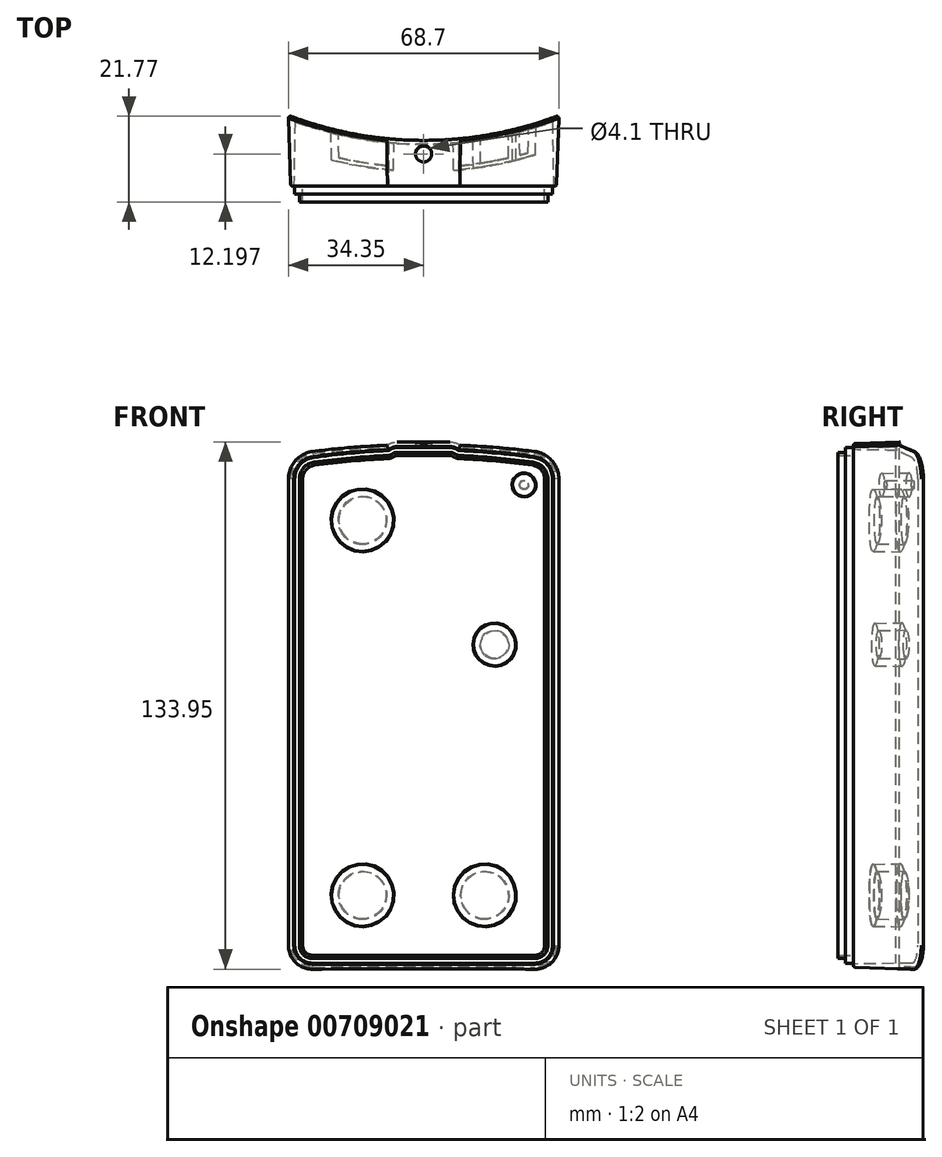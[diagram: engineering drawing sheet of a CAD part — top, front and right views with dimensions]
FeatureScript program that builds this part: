
annotation { "Feature Type Name" : "Feature", "Feature Type Description" : "" }
export const myFeature = defineFeature(function(context is Context, id is Id, definition is map)
    precondition{}
    {
        {
            var Q0;
            Q0=qCreatedBy(makeId("Front.planeOp"),FACE);
            var sketch = newSketch(context, id + "F0", { "sketchPlane" : qUnion([Q0])});
            skLineSegment(sketch, "E0.bottom", {"start": v(4.5, 0) * mm, "end": v(61, 0) * mm});
            skLineSegment(sketch, "E0.left", {"start": v(0, 4.5) * mm, "end": v(0, 123.05) * mm});
            skLineSegment(sketch, "E0.right", {"start": v(65.5, 4.5) * mm, "end": v(65.5, 123.05) * mm});
            skPoint(sketch, "E1.visualSharp", {"position": v(0, 0) * mm});
            skArc(sketch, "E1.filletArc", {"start": v(0, 4.5) * mm, "mid": v(1.32, 1.32) * mm, "end": v(4.5, 0) * mm});
            skPoint(sketch, "E2.visualSharp", {"position": v(65.5, 0) * mm});
            skArc(sketch, "E2.filletArc", {"start": v(61, 0) * mm, "mid": v(64.18, 1.32) * mm, "end": v(65.5, 4.5) * mm});
            skArc(sketch, "E3.filletArc", {"start": v(4.76, 128.5) * mm, "mid": v(1.36, 126.67) * mm, "end": v(0, 123.05) * mm});
            skPoint(sketch, "E4.visualSharp", {"position": v(65.5, 168.18) * mm});
            skArc(sketch, "E4.filletArc", {"start": v(65.5, 123.05) * mm, "mid": v(64.14, 126.67) * mm, "end": v(60.74, 128.5) * mm});
            skArc(sketch, "E5", {"start": v(60.74, 128.5) * mm, "mid": v(51.35, 129.57) * mm, "end": v(41.91, 130.2) * mm});
            skLineSegment(sketch, "E6", {"start": v(26, 131) * mm, "end": v(39.5, 131) * mm});
            skArc(sketch, "E7.trimOffspring", {"start": v(23.59, 130.2) * mm, "mid": v(14.15, 129.57) * mm, "end": v(4.76, 128.5) * mm});
            skLineSegment(sketch, "E8", {"start": v(32.75, 0) * mm, "end": v(32.75, 224.52) * mm, "construction": true});
            skArc(sketch, "E9", {"start": v(26, 131) * mm, "mid": v(25.02, 130.84) * mm, "end": v(24.13, 130.4) * mm});
            skPoint(sketch, "E10.visualSharp", {"position": v(23.91, 130.21) * mm});
            skArc(sketch, "E10.filletArc", {"start": v(23.59, 130.2) * mm, "mid": v(23.87, 130.26) * mm, "end": v(24.13, 130.4) * mm});
            skArc(sketch, "E11.MirrorCS", {"start": v(41.91, 130.2) * mm, "mid": v(41.63, 130.26) * mm, "end": v(41.37, 130.4) * mm});
            skArc(sketch, "E12.MirrorCS", {"start": v(39.5, 131) * mm, "mid": v(40.48, 130.84) * mm, "end": v(41.37, 130.4) * mm});
            skSolve(sketch);
        }
        {
            var Q0;
            Q0=qCreatedBy(makeId("Top.planeOp"),FACE);
            var sketch = newSketch(context, id + "F1", { "sketchPlane" : qUnion([Q0])});
            skArc(sketch, "E13", {"start": v(0, 0) * mm, "mid": v(32.75, -5.75) * mm, "end": v(65.5, 0) * mm});
            skLineSegment(sketch, "E14", {"start": v(0, 0) * mm, "end": v(65.5, 0) * mm});
            skLineSegment(sketch, "E15", {"start": v(0, 0) * mm, "end": v(94.5, 0) * mm, "construction": true});
            skLineSegment(sketch, "E16", {"start": v(94.5, 0) * mm, "end": v(32.75, 0) * mm, "construction": true});
            skLineSegment(sketch, "E17", {"start": v(32.75, 0) * mm, "end": v(32.75, -16.7) * mm, "construction": true});
            skSolve(sketch);
        }
        {
            var Q0;
            Q0=qSketchRegion(id+"F0",true);
            extrude(context, id + "F2", {"entities" : qUnion([Q0]), "depth" : 12.5 * mm, "offsetDistance" : 25 * mm});
        }
        {
            var Q0;
            Q0=qSketchRegion(id+"F1",true);
            extrude(context, id + "F3", {"entities" : qUnion([Q0]), "operationType" : NewBodyOperationType.REMOVE, "endBound" : BoundingType.THROUGH_ALL, "depth" : 25 * mm, "offsetDistance" : 25 * mm});
        }
        {
            var Q0;
            Q0=makeQuery(id+"F2.opExtrude","SWEPT_FACE",FACE,{"disambiguationData":[OSD([sQuery(id+"F0.wireOp",EDGE,"E0.bottom")])]});
            var sketch = newSketch(context, id + "F4", { "sketchPlane" : qUnion([Q0])});
            skLineSegment(sketch, "E18", {"start": v(0, 12.5) * mm, "end": v(0, 10.5) * mm});
            skLineSegment(sketch, "E19", {"start": v(0, 10.5) * mm, "end": v(1.1, 10.5) * mm});
            skLineSegment(sketch, "E20", {"start": v(1.1, 10.5) * mm, "end": v(1.1, 12.5) * mm});
            skLineSegment(sketch, "E21", {"start": v(1.1, 12.5) * mm, "end": v(0, 12.5) * mm});
            skSolve(sketch);
        }
        {
            var Q0;
            Q0=makeQuery(id+"F4.imprint","IMPRINT",FACE,{"disambiguationData":[TD([[makeQuery(id+"F4.imprint","IMPRINT",EDGE,{"derivedFrom":sQuery(id+"F4.wireOp",EDGE,"E18")}),1.0]])]});
            cPlane(context, id + "F5", {"entities" : qUnion([Q0]), "cplaneType" : CPlaneType.OFFSET, "offset" : 50 * mm, "oppositeDirection" : true, "width" : 150 * mm, "height" : 150 * mm});
        }
        {
            var Q0;
            Q0=makeQuery(id+"F2.opExtrude","CAP_FACE",FACE,{"disambiguationData":[OSD([sQuery(id+"F0.wireOp",EDGE,"E0.bottom"),sQuery(id+"F0.wireOp",EDGE,"E0.left"),sQuery(id+"F0.wireOp",EDGE,"E0.right"),sQuery(id+"F0.wireOp",EDGE,"E1.filletArc"),sQuery(id+"F0.wireOp",EDGE,"E2.filletArc"),sQuery(id+"F0.wireOp",EDGE,"E3.filletArc"),sQuery(id+"F0.wireOp",EDGE,"E4.filletArc"),sQuery(id+"F0.wireOp",EDGE,"E5"),sQuery(id+"F0.wireOp",EDGE,"E6"),sQuery(id+"F0.wireOp",EDGE,"4cuLOFSM-Cs9p-uLwk-Nxmp-eiNM5esqOte1"),sQuery(id+"F0.wireOp",EDGE,"qXNs2k06-4niP-ImqC-5Hru-JPzRlnRtqvzY"),sQuery(id+"F0.wireOp",EDGE,"592cab12-c6ad-4f12-8fa5-e9ea6a7a9ab5.filletArc"),sQuery(id+"F0.wireOp",EDGE,"E7.trimOffspring"),sQuery(id+"F0.wireOp",EDGE,"810a662d-7d86-4de4-b075-b749f1e53ed9.filletArc"),sQuery(id+"F0.wireOp",EDGE,"8d541c61-4af1-470d-ac14-312aa46fb37d.filletArc"),sQuery(id+"F0.wireOp",EDGE,"225b199f-dbc8-4900-9de2-33667acb90c7.filletArc")])],"isStart":false});
            shell(context, id + "F6", {"entities" : qUnion([Q0]), "thickness" : 2 * mm});
        }
        {
            var Q0;
            Q0=makeQuery(id+"F2.opExtrude","CAP_FACE",FACE,{"disambiguationData":[OSD([sQuery(id+"F0.wireOp",EDGE,"E0.bottom"),sQuery(id+"F0.wireOp",EDGE,"E0.left"),sQuery(id+"F0.wireOp",EDGE,"E0.right"),sQuery(id+"F0.wireOp",EDGE,"E1.filletArc"),sQuery(id+"F0.wireOp",EDGE,"E2.filletArc"),sQuery(id+"F0.wireOp",EDGE,"E3.filletArc"),sQuery(id+"F0.wireOp",EDGE,"E4.filletArc"),sQuery(id+"F0.wireOp",EDGE,"E5"),sQuery(id+"F0.wireOp",EDGE,"E6"),sQuery(id+"F0.wireOp",EDGE,"E7.trimOffspring"),sQuery(id+"F0.wireOp",EDGE,"E9"),sQuery(id+"F0.wireOp",EDGE,"E10.filletArc"),sQuery(id+"F0.wireOp",EDGE,"E11.MirrorCS"),sQuery(id+"F0.wireOp",EDGE,"E12.MirrorCS")])],"isStart":false});
            var sketch = newSketch(context, id + "F7", { "sketchPlane" : qUnion([Q0])});
            skLineSegment(sketch, "E22.0.0", {"start": v(39.5, 131) * mm, "end": v(26, 131) * mm});
            skArc(sketch, "E22.0.1", {"start": v(26, 131) * mm, "mid": v(25.02, 130.84) * mm, "end": v(24.13, 130.4) * mm});
            skArc(sketch, "E22.0.2", {"start": v(24.13, 130.4) * mm, "mid": v(23.87, 130.26) * mm, "end": v(23.59, 130.2) * mm});
            skArc(sketch, "E22.0.3", {"start": v(23.59, 130.2) * mm, "mid": v(14.15, 129.57) * mm, "end": v(4.76, 128.5) * mm});
            skArc(sketch, "E22.0.4", {"start": v(4.76, 128.5) * mm, "mid": v(1.36, 126.67) * mm, "end": v(0, 123.05) * mm});
            skLineSegment(sketch, "E22.0.5", {"start": v(0, 123.05) * mm, "end": v(0, 4.5) * mm});
            skArc(sketch, "E22.0.6", {"start": v(0, 4.5) * mm, "mid": v(1.32, 1.32) * mm, "end": v(4.5, 0) * mm});
            skLineSegment(sketch, "E22.0.7", {"start": v(4.5, 0) * mm, "end": v(61, 0) * mm});
            skArc(sketch, "E22.0.8", {"start": v(61, 0) * mm, "mid": v(64.18, 1.32) * mm, "end": v(65.5, 4.5) * mm});
            skLineSegment(sketch, "E22.0.9", {"start": v(65.5, 4.5) * mm, "end": v(65.5, 123.05) * mm});
            skArc(sketch, "E22.0.10", {"start": v(65.5, 123.05) * mm, "mid": v(64.14, 126.67) * mm, "end": v(60.74, 128.5) * mm});
            skArc(sketch, "E22.0.11", {"start": v(60.74, 128.5) * mm, "mid": v(51.35, 129.57) * mm, "end": v(41.91, 130.2) * mm});
            skArc(sketch, "E22.0.12", {"start": v(41.91, 130.2) * mm, "mid": v(41.63, 130.26) * mm, "end": v(41.37, 130.4) * mm});
            skArc(sketch, "E22.0.13", {"start": v(41.37, 130.4) * mm, "mid": v(40.48, 130.84) * mm, "end": v(39.5, 131) * mm});
            skArc(sketch, "E23.0", {"start": v(40.66, 129.42) * mm, "mid": v(40.1, 129.7) * mm, "end": v(39.5, 129.8) * mm});
            skArc(sketch, "E23.1", {"start": v(41.86, 129) * mm, "mid": v(41.23, 129.12) * mm, "end": v(40.66, 129.42) * mm});
            skArc(sketch, "E23.2", {"start": v(60.58, 127.31) * mm, "mid": v(51.24, 128.37) * mm, "end": v(41.86, 129) * mm});
            skArc(sketch, "E23.3", {"start": v(4.92, 127.31) * mm, "mid": v(2.26, 125.88) * mm, "end": v(1.2, 123.05) * mm});
            skArc(sketch, "E23.4", {"start": v(23.64, 129) * mm, "mid": v(14.26, 128.37) * mm, "end": v(4.92, 127.31) * mm});
            skArc(sketch, "E23.5", {"start": v(24.84, 129.42) * mm, "mid": v(24.27, 129.12) * mm, "end": v(23.64, 129) * mm});
            skArc(sketch, "E23.6", {"start": v(26, 129.8) * mm, "mid": v(25.4, 129.7) * mm, "end": v(24.84, 129.42) * mm});
            skLineSegment(sketch, "E23.7", {"start": v(1.2, 123.05) * mm, "end": v(1.2, 4.5) * mm});
            skArc(sketch, "E23.8", {"start": v(1.2, 4.5) * mm, "mid": v(2.17, 2.17) * mm, "end": v(4.5, 1.2) * mm});
            skLineSegment(sketch, "E23.9", {"start": v(4.5, 1.2) * mm, "end": v(61, 1.2) * mm});
            skLineSegment(sketch, "E23.10", {"start": v(39.5, 129.8) * mm, "end": v(26, 129.8) * mm});
            skArc(sketch, "E23.11", {"start": v(61, 1.2) * mm, "mid": v(63.33, 2.17) * mm, "end": v(64.3, 4.5) * mm});
            skLineSegment(sketch, "E23.12", {"start": v(64.3, 4.5) * mm, "end": v(64.3, 123.05) * mm});
            skArc(sketch, "E23.13", {"start": v(64.3, 123.05) * mm, "mid": v(63.24, 125.88) * mm, "end": v(60.58, 127.31) * mm});
            skSolve(sketch);
        }
        {
            var Q0;
            Q0=qSketchRegion(id+"F7",true);
            extrude(context, id + "F8", {"entities" : qUnion([Q0]), "operationType" : NewBodyOperationType.REMOVE, "oppositeDirection" : true, "depth" : 2 * mm, "offsetDistance" : 25 * mm});
        }
        {
            var Q0;
            Q0=makeQuery(id+"F6.opShell","OFFSET_EDGE",EDGE,{"disambiguationData":[OSD([sQuery(id+"F0.wireOp",EDGE,"E7.trimOffspring")])]});
            var Q1;
            Q1=makeQuery(id+"F8.boolean.opBoolean","COPY",EDGE,{"derivedFrom":makeQuery(id+"F8.opExtrude","CAP_EDGE",EDGE,{"disambiguationData":[OSD([sQuery(id+"F7.wireOp",EDGE,"E23.4")])],"isStart":true})});
            fillet(context, id + "F9", {"entities" : qUnion([Q0, Q1]), "radius" : .2 * mm, "tangentPropagation" : true, "allowEdgeOverflow" : false});
        }
        {
            var Q0;
            Q0=qCreatedBy(makeId("Front.planeOp"),FACE);
            var sketch = newSketch(context, id + "F10", { "sketchPlane" : qUnion([Q0])});
            skCircle(sketch, "E24", {"center": v(52.88, 68) * mm, "radius": 5.12 * mm});
            skArc(sketch, "E25", {"start": v(16.47, 64.05) * mm, "mid": v(12.44, 73) * mm, "end": v(9.49, 63.64) * mm});
            skArc(sketch, "E26", {"start": v(10.62, 44.32) * mm, "mid": v(14.94, 30.41) * mm, "end": v(17.6, 44.73) * mm});
            skLineSegment(sketch, "E27", {"start": v(12.75, 67.75) * mm, "end": v(14.5, 37.9) * mm, "construction": true});
            skLineSegment(sketch, "E28", {"start": v(16.47, 64.05) * mm, "end": v(17.6, 44.73) * mm});
            skLineSegment(sketch, "E29.MirrorCS", {"start": v(9.49, 63.64) * mm, "end": v(10.62, 44.32) * mm});
            skSolve(sketch);
        }
        {
            var Q0;
            Q0=qSketchRegion(id+"F10",true);
            extrude(context, id + "F11", {"entities" : qUnion([Q0]), "operationType" : NewBodyOperationType.REMOVE, "endBound" : BoundingType.THROUGH_ALL, "depth" : 25 * mm, "offsetDistance" : 25 * mm});
        }
        {
            var Q0;
            Q0=qCreatedBy(makeId("Front.planeOp"),FACE);
            var sketch = newSketch(context, id + "F12", { "sketchPlane" : qUnion([Q0])});
            skLineSegment(sketch, "E30", {"start": v(51.75, 114.46) * mm, "end": v(32.54, 67.75) * mm, "construction": true});
            skArc(sketch, "E31.0.startCap", {"start": v(49.2, 115.5) * mm, "mid": v(52.8, 117) * mm, "end": v(54.3, 113.41) * mm});
            skArc(sketch, "E31.0.endCap", {"start": v(35.09, 66.7) * mm, "mid": v(31.5, 65.2) * mm, "end": v(30, 68.8) * mm});
            skLineSegment(sketch, "E31.0.left", {"start": v(54.3, 113.41) * mm, "end": v(35.09, 66.7) * mm});
            skLineSegment(sketch, "E31.0.right", {"start": v(49.2, 115.5) * mm, "end": v(30, 68.8) * mm});
            skLineSegment(sketch, "E32.0", {"start": v(48.28, 115.89) * mm, "end": v(29.08, 69.18) * mm});
            skArc(sketch, "E32.1", {"start": v(48.28, 115.89) * mm, "mid": v(53.18, 117.93) * mm, "end": v(55.22, 113.03) * mm});
            skLineSegment(sketch, "E32.2", {"start": v(55.22, 113.03) * mm, "end": v(36.01, 66.32) * mm});
            skArc(sketch, "E32.3", {"start": v(36.01, 66.32) * mm, "mid": v(31.12, 64.28) * mm, "end": v(29.08, 69.18) * mm});
            skSolve(sketch);
        }
        {
            var Q0;
            {var subQ0=sQuery(id+"F1.wireOp",EDGE,"E14");var subQ1=sQuery(id+"F1.wireOp",EDGE,"E13");Q0=makeQuery(id+"F3.boolean.opBoolean","MERGE",EDGE,{"derivedFrom":[makeQuery(id+"F2.opExtrude","CAP_EDGE",EDGE,{"disambiguationData":[OSD([sQuery(id+"F0.wireOp",EDGE,"E0.left")])],"isStart":true}),makeQuery(id+"F3.opExtrude","SWEPT_EDGE",EDGE,{"disambiguationData":[OSD([subQ1,subQ0]),TDD([makeQuery(id+"F1.imprint","INTERSECT",VERTEX,{"disambiguationData":[OD(0.0)],"derivedFrom":[subQ1,subQ0]})])]})]});}
            fillet(context, id + "F13", {"entities" : qUnion([Q0]), "radius" : .5 * mm, "tangentPropagation" : true, "allowEdgeOverflow" : false});
        }
        {
            var Q0;
            Q0=qSketchRegion(id+"F12",true);
            var Q1;
            Q1=makeQuery(id+"F3.boolean.opBoolean","COPY",FACE,{"derivedFrom":makeQuery(id+"F3.opExtrude","SWEPT_FACE",FACE,{"disambiguationData":[OSD([sQuery(id+"F1.wireOp",EDGE,"E13")])]})});
            var Q2;
            Q2=makeQuery(id+"F2.opExtrude","SWEPT_BODY",BODY,{"disambiguationData":[OSD([sQuery(id+"F0.wireOp",EDGE,"E0.bottom"),sQuery(id+"F0.wireOp",EDGE,"E0.left"),sQuery(id+"F0.wireOp",EDGE,"E0.right"),sQuery(id+"F0.wireOp",EDGE,"E1.filletArc"),sQuery(id+"F0.wireOp",EDGE,"E2.filletArc"),sQuery(id+"F0.wireOp",EDGE,"E3.filletArc"),sQuery(id+"F0.wireOp",EDGE,"E4.filletArc"),sQuery(id+"F0.wireOp",EDGE,"E5"),sQuery(id+"F0.wireOp",EDGE,"E6"),sQuery(id+"F0.wireOp",EDGE,"E7.trimOffspring"),sQuery(id+"F0.wireOp",EDGE,"E9"),sQuery(id+"F0.wireOp",EDGE,"E10.filletArc"),sQuery(id+"F0.wireOp",EDGE,"E11.MirrorCS"),sQuery(id+"F0.wireOp",EDGE,"E12.MirrorCS")])]});
            var Q3;
            Q3=makeQuery(id+"F3.boolean.opBoolean","COPY",FACE,{"derivedFrom":makeQuery(id+"F3.opExtrude","SWEPT_FACE",FACE,{"disambiguationData":[OSD([sQuery(id+"F1.wireOp",EDGE,"E13")])]})});
            extrude(context, id + "F14", {"entities" : qUnion([Q0]), "operationType" : NewBodyOperationType.ADD, "endBound" : BoundingType.UP_TO_SURFACE, "depth" : 25 * mm, "endBoundEntityFace" : qUnion([Q1]), "endBoundEntityBody" : qUnion([Q2]), "offsetDistance" : 1 * mm, "offsetOppositeDirection" : true, "hasSecondDirection" : true, "secondDirectionBound" : BoundingType.UP_TO_SURFACE, "secondDirectionOppositeDirection" : false, "secondDirectionDepth" : 1 * mm, "secondDirectionBoundEntityFace" : qUnion([Q3]), "hasSecondDirectionOffset" : true, "secondDirectionOffsetDistance" : .5 * mm});
        }
        {
            var Q0;
            Q0=makeQuery(id+"F14.opExtrude","CAP_EDGE",EDGE,{"disambiguationData":[OSD([sQuery(id+"F12.wireOp",EDGE,"E31.0.left")])],"isStart":true});
            var Q1;
            Q1=makeQuery(id+"F14.opExtrude","CAP_EDGE",EDGE,{"disambiguationData":[OSD([sQuery(id+"F12.wireOp",EDGE,"E32.2")])],"isStart":true});
            fillet(context, id + "F15", {"entities" : qUnion([Q0, Q1]), "radius" : .5 * mm, "tangentPropagation" : true, "allowEdgeOverflow" : false});
        }
        {
            var Q0;
            Q0=qCreatedBy(makeId("Front.planeOp"),FACE);
            var sketch = newSketch(context, id + "F16", { "sketchPlane" : qUnion([Q0])});
            skCircle(sketch, "E33", {"center": v(51.75, 114.46) * mm, "radius": 0.75 * mm});
            skLineSegment(sketch, "E34.0", {"start": v(51.75, 114.46) * mm, "end": v(32.54, 67.75) * mm, "construction": true});
            skSolve(sketch);
        }
        {
            var Q0;
            Q0=makeQuery(id+"F16.imprint","IMPRINT",FACE,{"disambiguationData":[TD([[makeQuery(id+"F16.imprint","IMPRINT",EDGE,{"derivedFrom":sQuery(id+"F16.wireOp",EDGE,"E33")}),1.0]])]});
            var Q1;
            Q1=qConstructionFilter(qBodyType(qCreatedBy(id+"F16",EDGE),BodyType.WIRE),ConstructionObject.NO);
            extrude(context, id + "F17", {"entities" : qUnion([Q0]), "operationType" : NewBodyOperationType.REMOVE, "surfaceEntities" : qUnion([Q1]), "endBound" : BoundingType.THROUGH_ALL, "depth" : 25 * mm, "offsetDistance" : 25 * mm});
        }
        {
            var Q0;
            Q0=qCreatedBy(makeId("Top.planeOp"),FACE);
            var sketch = newSketch(context, id + "F18", { "sketchPlane" : qUnion([Q0])});
            skLineSegment(sketch, "E35.0", {"start": v(-0.5, -7.5) * mm, "end": v(-0.5, 1.21) * mm});
            skLineSegment(sketch, "E35.1", {"start": v(66, -7.57) * mm, "end": v(66, 1.14) * mm});
            skLineSegment(sketch, "E36", {"start": v(32.75, -4) * mm, "end": v(32.75, 0.99) * mm, "construction": true});
            skPoint(sketch, "E36.startSnap0", {"position": v(32.75, -4) * mm});
            skArc(sketch, "E37.0", {"start": v(66, 1.14) * mm, "mid": v(32.75, -4.75) * mm, "end": v(-0.5, 1.21) * mm});
            skSolve(sketch);
        }
        {
            var Q0;
            Q0=makeQuery(id+"F8.boolean.opBoolean","COPY",FACE,{"derivedFrom":makeQuery(id+"F8.opExtrude","CAP_FACE",FACE,{"disambiguationData":[OSD([sQuery(id+"F7.wireOp",EDGE,"E22.0.0"),sQuery(id+"F7.wireOp",EDGE,"E22.0.1"),sQuery(id+"F7.wireOp",EDGE,"E22.0.2"),sQuery(id+"F7.wireOp",EDGE,"E22.0.3"),sQuery(id+"F7.wireOp",EDGE,"E22.0.4"),sQuery(id+"F7.wireOp",EDGE,"E22.0.5"),sQuery(id+"F7.wireOp",EDGE,"E22.0.6"),sQuery(id+"F7.wireOp",EDGE,"E22.0.7"),sQuery(id+"F7.wireOp",EDGE,"E22.0.8"),sQuery(id+"F7.wireOp",EDGE,"E22.0.9"),sQuery(id+"F7.wireOp",EDGE,"E22.0.10"),sQuery(id+"F7.wireOp",EDGE,"E22.0.11"),sQuery(id+"F7.wireOp",EDGE,"E22.0.12"),sQuery(id+"F7.wireOp",EDGE,"E22.0.13"),sQuery(id+"F7.wireOp",EDGE,"E23.0"),sQuery(id+"F7.wireOp",EDGE,"E23.1"),sQuery(id+"F7.wireOp",EDGE,"E23.2"),sQuery(id+"F7.wireOp",EDGE,"E23.3"),sQuery(id+"F7.wireOp",EDGE,"E23.4"),sQuery(id+"F7.wireOp",EDGE,"E23.5"),sQuery(id+"F7.wireOp",EDGE,"E23.6"),sQuery(id+"F7.wireOp",EDGE,"E23.7"),sQuery(id+"F7.wireOp",EDGE,"E23.8"),sQuery(id+"F7.wireOp",EDGE,"E23.9"),sQuery(id+"F7.wireOp",EDGE,"E23.10"),sQuery(id+"F7.wireOp",EDGE,"E23.11"),sQuery(id+"F7.wireOp",EDGE,"E23.12"),sQuery(id+"F7.wireOp",EDGE,"E23.13")])],"isStart":false})});
            cPlane(context, id + "F19", {"entities" : qUnion([Q0]), "cplaneType" : CPlaneType.OFFSET, "offset" : 2 * mm, "oppositeDirection" : true, "width" : 150 * mm, "height" : 150 * mm});
        }
        {
            var Q0;
            Q0=qCreatedBy(id+"F19.planeOp",FACE);
            var sketch = newSketch(context, id + "F20", { "sketchPlane" : qUnion([Q0])});
            skLineSegment(sketch, "E38.0.0", {"start": v(39.5, 131) * mm, "end": v(26, 131) * mm});
            skArc(sketch, "E38.0.1", {"start": v(26, 131) * mm, "mid": v(25.02, 130.84) * mm, "end": v(24.13, 130.4) * mm});
            skArc(sketch, "E38.0.2", {"start": v(24.13, 130.4) * mm, "mid": v(23.87, 130.26) * mm, "end": v(23.59, 130.2) * mm});
            skArc(sketch, "E38.0.3", {"start": v(23.59, 130.2) * mm, "mid": v(14.15, 129.57) * mm, "end": v(4.76, 128.5) * mm});
            skArc(sketch, "E38.0.4", {"start": v(4.76, 128.5) * mm, "mid": v(1.36, 126.67) * mm, "end": v(0, 123.05) * mm});
            skLineSegment(sketch, "E38.0.5", {"start": v(0, 123.05) * mm, "end": v(0, 4.5) * mm});
            skArc(sketch, "E38.0.6", {"start": v(0, 4.5) * mm, "mid": v(1.32, 1.32) * mm, "end": v(4.5, 0) * mm});
            skLineSegment(sketch, "E38.0.7", {"start": v(4.5, 0) * mm, "end": v(61, 0) * mm});
            skArc(sketch, "E38.0.8", {"start": v(61, 0) * mm, "mid": v(64.18, 1.32) * mm, "end": v(65.5, 4.5) * mm});
            skLineSegment(sketch, "E38.0.9", {"start": v(65.5, 4.5) * mm, "end": v(65.5, 123.05) * mm});
            skArc(sketch, "E38.0.10", {"start": v(65.5, 123.05) * mm, "mid": v(64.14, 126.67) * mm, "end": v(60.74, 128.5) * mm});
            skArc(sketch, "E38.0.11", {"start": v(60.74, 128.5) * mm, "mid": v(51.35, 129.57) * mm, "end": v(41.91, 130.2) * mm});
            skArc(sketch, "E38.0.12", {"start": v(41.91, 130.2) * mm, "mid": v(41.63, 130.26) * mm, "end": v(41.37, 130.4) * mm});
            skArc(sketch, "E38.0.13", {"start": v(41.37, 130.4) * mm, "mid": v(40.48, 130.84) * mm, "end": v(39.5, 131) * mm});
            skLineSegment(sketch, "E39.0", {"start": v(4.5, -1) * mm, "end": v(61, -1) * mm});
            skArc(sketch, "E39.1", {"start": v(41.96, 131.2) * mm, "mid": v(40.8, 131.8) * mm, "end": v(39.5, 132) * mm});
            skArc(sketch, "E39.2", {"start": v(60.88, 129.5) * mm, "mid": v(51.44, 130.56) * mm, "end": v(41.96, 131.2) * mm});
            skArc(sketch, "E39.3", {"start": v(66.5, 123.05) * mm, "mid": v(64.9, 127.32) * mm, "end": v(60.88, 129.5) * mm});
            skLineSegment(sketch, "E39.4", {"start": v(66.5, 4.5) * mm, "end": v(66.5, 123.05) * mm});
            skLineSegment(sketch, "E39.5", {"start": v(39.5, 132) * mm, "end": v(26, 132) * mm});
            skArc(sketch, "E39.6", {"start": v(61, -1) * mm, "mid": v(64.89, 0.61) * mm, "end": v(66.5, 4.5) * mm});
            skArc(sketch, "E39.7", {"start": v(26, 132) * mm, "mid": v(24.7, 131.8) * mm, "end": v(23.54, 131.2) * mm});
            skArc(sketch, "E39.8", {"start": v(23.54, 131.2) * mm, "mid": v(14.06, 130.56) * mm, "end": v(4.62, 129.5) * mm});
            skArc(sketch, "E39.9", {"start": v(4.62, 129.5) * mm, "mid": v(0.6, 127.32) * mm, "end": v(-1, 123.05) * mm});
            skLineSegment(sketch, "E39.10", {"start": v(-1, 123.05) * mm, "end": v(-1, 4.5) * mm});
            skArc(sketch, "E39.11", {"start": v(-1, 4.5) * mm, "mid": v(0.61, 0.61) * mm, "end": v(4.5, -1) * mm});
            skArc(sketch, "E40.0", {"start": v(4.72, 128.75) * mm, "mid": v(1.17, 126.83) * mm, "end": v(-0.25, 123.05) * mm});
            skLineSegment(sketch, "E40.1", {"start": v(65.75, 4.5) * mm, "end": v(65.75, 123.05) * mm});
            skArc(sketch, "E40.2", {"start": v(61, -0.25) * mm, "mid": v(64.36, 1.14) * mm, "end": v(65.75, 4.5) * mm});
            skLineSegment(sketch, "E40.3", {"start": v(4.5, -0.25) * mm, "end": v(61, -0.25) * mm});
            skArc(sketch, "E40.4", {"start": v(-0.25, 4.5) * mm, "mid": v(1.14, 1.14) * mm, "end": v(4.5, -0.25) * mm});
            skArc(sketch, "E40.5", {"start": v(65.75, 123.05) * mm, "mid": v(64.33, 126.83) * mm, "end": v(60.78, 128.75) * mm});
            skLineSegment(sketch, "E40.6", {"start": v(-0.25, 123.05) * mm, "end": v(-0.25, 4.5) * mm});
            skArc(sketch, "E40.7", {"start": v(60.78, 128.75) * mm, "mid": v(51.25, 129.82) * mm, "end": v(41.68, 130.46) * mm});
            skArc(sketch, "E40.8", {"start": v(41.68, 130.46) * mm, "mid": v(40.66, 131.05) * mm, "end": v(39.5, 131.25) * mm});
            skLineSegment(sketch, "E40.9", {"start": v(39.5, 131.25) * mm, "end": v(26, 131.25) * mm});
            skArc(sketch, "E40.10", {"start": v(26, 131.25) * mm, "mid": v(24.84, 131.05) * mm, "end": v(23.82, 130.46) * mm});
            skArc(sketch, "E40.11", {"start": v(23.82, 130.46) * mm, "mid": v(14.25, 129.82) * mm, "end": v(4.72, 128.75) * mm});
            skSolve(sketch);
        }
        {
            var Q0;
            Q0=makeQuery(id+"F20.imprint","IMPRINT",FACE,{"disambiguationData":[TD([[makeQuery(id+"F20.imprint","IMPRINT",EDGE,{"derivedFrom":sQuery(id+"F20.wireOp",EDGE,"E38.0.0")}),-1.0]])]});
            var Q1;
            Q1=makeQuery(id+"F20.imprint","IMPRINT",FACE,{"disambiguationData":[TD([[makeQuery(id+"F20.imprint","IMPRINT",EDGE,{"derivedFrom":sQuery(id+"F20.wireOp",EDGE,"E38.0.0")}),1.0]])]});
            var Q2;
            Q2=makeQuery(id+"F20.imprint","IMPRINT",FACE,{"disambiguationData":[TD([[makeQuery(id+"F20.imprint","IMPRINT",EDGE,{"derivedFrom":sQuery(id+"F20.wireOp",EDGE,"E39.0")}),1.0]])]});
            extrude(context, id + "F21", {"entities" : qUnion([Q0, Q1, Q2]), "oppositeDirection" : true, "depth" : 18 * mm, "offsetDistance" : 25 * mm, "hasDraft" : true, "draftAngle" : 2 * degree});
        }
        {
            var Q0;
            Q0=qCreatedBy(makeId("Top.planeOp"),FACE);
            var sketch = newSketch(context, id + "F22", { "sketchPlane" : qUnion([Q0])});
            skLineSegment(sketch, "E41.0.0", {"start": v(61, -8.5) * mm, "end": v(4.5, -8.5) * mm, "construction": true});
            skLineSegment(sketch, "E41.0.1", {"start": v(4.5, 9.5) * mm, "end": v(4.5, -8.5) * mm, "construction": true});
            skLineSegment(sketch, "E41.0.2", {"start": v(4.5, 9.5) * mm, "end": v(61, 9.5) * mm, "construction": true});
            skLineSegment(sketch, "E41.0.3", {"start": v(61, 9.5) * mm, "end": v(61, -8.5) * mm, "construction": true});
            skLineSegment(sketch, "E41.1.0", {"start": v(66.5, -8.5) * mm, "end": v(61, -8.5) * mm, "construction": true});
            skLineSegment(sketch, "E41.1.1", {"start": v(61, 9.5) * mm, "end": v(61, -8.5) * mm, "construction": true});
            skLineSegment(sketch, "E41.1.2", {"start": v(61, 9.5) * mm, "end": v(67.13, 9.5) * mm, "construction": true});
            skLineSegment(sketch, "E41.1.3", {"start": v(67.13, 9.5) * mm, "end": v(66.5, -8.5) * mm, "construction": true});
            skLineSegment(sketch, "E41.2.0", {"start": v(4.5, -8.5) * mm, "end": v(-1, -8.5) * mm, "construction": true});
            skLineSegment(sketch, "E41.2.1", {"start": v(-1.63, 9.5) * mm, "end": v(-1, -8.5) * mm, "construction": true});
            skLineSegment(sketch, "E41.2.2", {"start": v(-1.63, 9.5) * mm, "end": v(4.5, 9.5) * mm, "construction": true});
            skLineSegment(sketch, "E41.2.3", {"start": v(4.5, 9.5) * mm, "end": v(4.5, -8.5) * mm, "construction": true});
            skArc(sketch, "E42", {"start": v(-1.63, 9.5) * mm, "mid": v(32.75, 3.14) * mm, "end": v(67.13, 9.5) * mm});
            skLineSegment(sketch, "E43", {"start": v(-1.63, 9.5) * mm, "end": v(67.13, 9.5) * mm});
            skSolve(sketch);
        }
        {
            var Q0;
            Q0=makeQuery(id+"F22.imprint","IMPRINT",FACE,{"disambiguationData":[TD([[makeQuery(id+"F22.imprint","IMPRINT",EDGE,{"derivedFrom":sQuery(id+"F22.wireOp",EDGE,"E42")}),1.0]])]});
            extrude(context, id + "F23", {"entities" : qUnion([Q0]), "operationType" : NewBodyOperationType.REMOVE, "endBound" : BoundingType.THROUGH_ALL, "oppositeDirection" : true, "depth" : 25 * mm, "offsetDistance" : 25 * mm, "hasSecondDirection" : true, "secondDirectionBound" : BoundingType.THROUGH_ALL, "secondDirectionOppositeDirection" : false, "secondDirectionDepth" : 25 * mm});
        }
        {
            var Q0;
            Q0=qCreatedBy(makeId("Top.planeOp"),FACE);
            cPlane(context, id + "F24", {"entities" : qUnion([Q0]), "cplaneType" : CPlaneType.OFFSET, "offset" : 6.5 * mm, "oppositeDirection" : true, "width" : 150 * mm, "height" : 150 * mm});
        }
        {
            var Q0;
            Q0=sQuery(id+"F18.wireOp",EDGE,"E37.0");
            extrude(context, id + "F25", {"bodyType" : ToolBodyType.SURFACE, "surfaceEntities" : qUnion([Q0]), "oppositeDirection" : true, "depth" : 5 * mm, "offsetDistance" : 25 * mm, "hasSecondDirection" : true, "secondDirectionOppositeDirection" : false, "secondDirectionDepth" : 150 * mm});
        }
        {
            var Q0;
            Q0=qCreatedBy(id+"F24.planeOp",FACE);
            var sketch = newSketch(context, id + "F26", { "sketchPlane" : qUnion([Q0])});
            skArc(sketch, "E44.0", {"start": v(-0.75, 1.9) * mm, "mid": v(32.75, -4.13) * mm, "end": v(66.25, 1.9) * mm});
            skLineSegment(sketch, "E45.0.0", {"start": v(39.5, -10.5) * mm, "end": v(39.5, -6.01) * mm, "construction": true});
            skArc(sketch, "E45.0.1", {"start": v(39.5, -6.01) * mm, "mid": v(32.75, -6.25) * mm, "end": v(26, -6.01) * mm, "construction": true});
            skLineSegment(sketch, "E45.0.2", {"start": v(26, -6.01) * mm, "end": v(26, -10.5) * mm, "construction": true});
            skLineSegment(sketch, "E45.0.3", {"start": v(26, -10.5) * mm, "end": v(39.5, -10.5) * mm, "construction": true});
            skLineSegment(sketch, "E46", {"start": v(32.75, -10.5) * mm, "end": v(32.75, 21.11) * mm, "construction": true});
            skPoint(sketch, "E46.endSnap0", {"position": v(32.75, -6.25) * mm});
            skSolve(sketch);
        }
        {
            var Q0;
            Q0=sQuery(id+"F26.wireOp",EDGE,"E44.0");
            extrude(context, id + "F27", {"bodyType" : ToolBodyType.SURFACE, "surfaceEntities" : qUnion([Q0]), "depth" : 147.2 * mm, "offsetDistance" : 25 * mm});
        }
        {
            var Q0;
            Q0=qCreatedBy(makeId("Front.planeOp"),FACE);
            cPlane(context, id + "F28", {"entities" : qUnion([Q0]), "cplaneType" : CPlaneType.OFFSET, "offset" : 10 * mm, "oppositeDirection" : true, "width" : 150 * mm, "height" : 150 * mm});
        }
        {
            var Q0;
            Q0=sQuery(id+"F22.wireOp",EDGE,"E42");
            extrude(context, id + "F29", {"bodyType" : ToolBodyType.SURFACE, "surfaceEntities" : qUnion([Q0]), "oppositeDirection" : true, "depth" : 10 * mm, "offsetDistance" : 25 * mm, "hasSecondDirection" : true, "secondDirectionOppositeDirection" : false, "secondDirectionDepth" : 141.6 * mm});
        }
        {
            var Q0;
            Q0=makeQuery(id+"F29.opExtrude","SWEPT_BODY",BODY,{"disambiguationData":[OSD([sQuery(id+"F22.wireOp",EDGE,"E42")])]});
            transform(context, id + "F30", {"entities" : qUnion([Q0]), "transformType" : TransformType.TRANSLATION_3D, "dx" : 0 * mm, "dy" : -1 * mm, "dz" : 0 * mm, "makeCopy" : false});
        }
        {
            var Q0;
            Q0=qCreatedBy(makeId("Top.planeOp"),FACE);
            cPlane(context, id + "F31", {"entities" : qUnion([Q0]), "cplaneType" : CPlaneType.OFFSET, "offset" : 140.2 * mm, "width" : 150 * mm, "height" : 150 * mm});
        }
        {
            var Q0;
            Q0=qCreatedBy(id+"F31.planeOp",FACE);
            var sketch = newSketch(context, id + "F32", { "sketchPlane" : qUnion([Q0])});
            skLineSegment(sketch, "E47.0.0", {"start": v(26, 3.38) * mm, "end": v(26, -6.5) * mm, "construction": true});
            skLineSegment(sketch, "E47.0.1", {"start": v(26, -6.5) * mm, "end": v(39.5, -6.5) * mm, "construction": true});
            skLineSegment(sketch, "E47.0.2", {"start": v(39.5, 3.38) * mm, "end": v(39.5, -6.5) * mm, "construction": true});
            skArc(sketch, "E47.0.3", {"start": v(36, 3.2) * mm, "mid": v(32.75, 3.14) * mm, "end": v(29.5, 3.2) * mm});
            skLineSegment(sketch, "E48", {"start": v(32.75, -6.5) * mm, "end": v(32.75, 3.14) * mm, "construction": true});
            skLineSegment(sketch, "E49", {"start": v(29.5, 3.2) * mm, "end": v(29.5, -0.1) * mm});
            skLineSegment(sketch, "E50.MirrorCS", {"start": v(36, 3.2) * mm, "end": v(36, -0.1) * mm});
            skArc(sketch, "E51", {"start": v(29.5, -0.1) * mm, "mid": v(32.75, -3.36) * mm, "end": v(36, -0.1) * mm});
            skSolve(sketch);
        }
        {
            var Q0;
            Q0=makeQuery(id+"F21.opExtrude","CAP_EDGE",EDGE,{"disambiguationData":[OSD([sQuery(id+"F20.wireOp",EDGE,"E39.2")])],"isStart":true});
            var Q1;
            Q1=makeQuery(id+"F21.opExtrude","CAP_EDGE",EDGE,{"disambiguationData":[OSD([sQuery(id+"F20.wireOp",EDGE,"E39.1")])],"isStart":true});
            fillet(context, id + "F33", {"entities" : qUnion([Q0, Q1]), "radius" : .5 * mm, "tangentPropagation" : true, "allowEdgeOverflow" : false});
        }
        {
            var Q0;
            Q0=qCreatedBy(makeId("Front.planeOp"),FACE);
            var sketch = newSketch(context, id + "F34", { "sketchPlane" : qUnion([Q0])});
            skArc(sketch, "E52.0", {"start": v(36, 115.24) * mm, "mid": v(32.75, 115.26) * mm, "end": v(29.5, 115.24) * mm});
            skArc(sketch, "E53", {"start": v(29.5, 115.24) * mm, "mid": v(32.75, 112.01) * mm, "end": v(36, 115.24) * mm});
            skSolve(sketch);
        }
        {
            var Q0;
            Q0=makeQuery(id+"F20.imprint","IMPRINT",FACE,{"disambiguationData":[TD([[makeQuery(id+"F20.imprint","IMPRINT",EDGE,{"derivedFrom":sQuery(id+"F20.wireOp",EDGE,"E38.0.0")}),-1.0]])]});
            var Q1;
            Q1=makeQuery(id+"F20.imprint","IMPRINT",FACE,{"disambiguationData":[TD([[makeQuery(id+"F20.imprint","IMPRINT",EDGE,{"derivedFrom":sQuery(id+"F20.wireOp",EDGE,"E38.0.0")}),1.0]])]});
            var Q2;
            Q2=makeQuery(id+"F29.opExtrude","SWEPT_FACE",FACE,{"disambiguationData":[OSD([sQuery(id+"F22.wireOp",EDGE,"E42")])]});
            extrude(context, id + "F35", {"entities" : qUnion([Q0, Q1]), "operationType" : NewBodyOperationType.REMOVE, "endBound" : BoundingType.UP_TO_SURFACE, "oppositeDirection" : true, "depth" : 25 * mm, "endBoundEntityFace" : qUnion([Q2]), "offsetDistance" : 25 * mm, "hasDraft" : true, "draftAngle" : 1 * degree, "draftPullDirection" : true});
        }
        {
            var Q0;
            Q0=qCreatedBy(makeId("Front.planeOp"),FACE);
            cPlane(context, id + "F36", {"entities" : qUnion([Q0]), "cplaneType" : CPlaneType.OFFSET, "offset" : 25 * mm, "width" : 150 * mm, "height" : 150 * mm});
        }
        {
            var Q0;
            Q0=qCreatedBy(id+"F36.planeOp",FACE);
            var sketch = newSketch(context, id + "F37", { "sketchPlane" : qUnion([Q0])});
            skCircle(sketch, "E54", {"center": v(48.25, 17.25) * mm, "radius": 7.5 * mm});
            skLineSegment(sketch, "E55.0", {"start": v(4.5, -0.52) * mm, "end": v(61, -0.52) * mm, "construction": true});
            skLineSegment(sketch, "E56", {"start": v(32.75, -0.52) * mm, "end": v(32.75, 50.45) * mm, "construction": true});
            skCircle(sketch, "E57.MirrorC", {"center": v(17.25, 17.25) * mm, "radius": 7.5 * mm});
            skCircle(sketch, "E58.MirrorC", {"center": v(17.25, 112.52) * mm, "radius": 7.5 * mm});
            skCircle(sketch, "E59", {"center": v(50.75, 80.95) * mm, "radius": 5 * mm});
            skCircle(sketch, "E60", {"center": v(58.25, 121.52) * mm, "radius": 2.5 * mm});
            skSolve(sketch);
        }
        {
            var Q0;
            Q0=qSketchRegion(id+"F37",true);
            var Q1;
            Q1=makeQuery(id+"F21.opExtrude","SWEPT_BODY",BODY,{"disambiguationData":[OSD([sQuery(id+"F20.wireOp",EDGE,"E39.0"),sQuery(id+"F20.wireOp",EDGE,"E39.1"),sQuery(id+"F20.wireOp",EDGE,"E39.2"),sQuery(id+"F20.wireOp",EDGE,"E39.3"),sQuery(id+"F20.wireOp",EDGE,"E39.4"),sQuery(id+"F20.wireOp",EDGE,"E39.5"),sQuery(id+"F20.wireOp",EDGE,"E39.6"),sQuery(id+"F20.wireOp",EDGE,"E39.7"),sQuery(id+"F20.wireOp",EDGE,"E39.8"),sQuery(id+"F20.wireOp",EDGE,"E39.9"),sQuery(id+"F20.wireOp",EDGE,"E39.10"),sQuery(id+"F20.wireOp",EDGE,"E39.11")])]});
            var Q2;
            Q2=makeQuery(id+"F25.opExtrude","SWEPT_FACE",FACE,{"disambiguationData":[OSD([sQuery(id+"F18.wireOp",EDGE,"E37.0")])]});
            extrude(context, id + "F38", {"entities" : qUnion([Q0]), "operationType" : NewBodyOperationType.ADD, "endBound" : BoundingType.UP_TO_BODY, "oppositeDirection" : true, "depth" : 25 * mm, "endBoundEntityBody" : qUnion([Q1]), "offsetDistance" : 25 * mm, "hasDraft" : true, "draftAngle" : 1 * degree, "hasSecondDirection" : true, "secondDirectionBound" : BoundingType.UP_TO_SURFACE, "secondDirectionOppositeDirection" : true, "secondDirectionDepth" : 25 * mm, "secondDirectionBoundEntityFace" : qUnion([Q2])});
        }
        {
            var Q0;
            Q0=qCreatedBy(makeId("Front.planeOp"),FACE);
            cPlane(context, id + "F39", {"entities" : qUnion([Q0]), "cplaneType" : CPlaneType.OFFSET, "offset" : 25 * mm, "oppositeDirection" : true, "width" : 150 * mm, "height" : 150 * mm});
        }
        {
            var Q0;
            Q0=qCreatedBy(id+"F39.planeOp",FACE);
            var sketch = newSketch(context, id + "F40", { "sketchPlane" : qUnion([Q0])});
            skCircle(sketch, "E61.0", {"center": v(17.25, 112.52) * mm, "radius": 6.5 * mm});
            skCircle(sketch, "E61.1", {"center": v(58.25, 121.52) * mm, "radius": 1.5 * mm});
            skCircle(sketch, "E61.2", {"center": v(50.75, 80.95) * mm, "radius": 4 * mm});
            skCircle(sketch, "E61.3", {"center": v(48.25, 17.25) * mm, "radius": 6.5 * mm});
            skLineSegment(sketch, "E61.4", {"start": v(32.75, -0.52) * mm, "end": v(32.75, 50.45) * mm, "construction": true});
            skCircle(sketch, "E61.5", {"center": v(17.25, 17.25) * mm, "radius": 6.5 * mm});
            skLineSegment(sketch, "E61.6", {"start": v(4.5, -0.52) * mm, "end": v(61, -0.52) * mm, "construction": true});
            skSolve(sketch);
        }
        {
            var Q0;
            Q0=qSketchRegion(id+"F40",true);
            var Q1;
            Q1=makeQuery(id+"F38.opExtrude","CAP_FACE",FACE,{"disambiguationData":[OSD([sQuery(id+"F37.wireOp",EDGE,"E58.MirrorC")]),topologyDisambiguationEdgeConnected([makeQuery(id+"F25.opExtrude","SWEPT_FACE",FACE,{"disambiguationData":[OSD([sQuery(id+"F18.wireOp",EDGE,"E37.0")])]})])],"isStart":false});
            extrude(context, id + "F41", {"entities" : qUnion([Q0]), "operationType" : NewBodyOperationType.REMOVE, "endBound" : BoundingType.UP_TO_SURFACE, "depth" : 25 * mm, "endBoundEntityFace" : qUnion([Q1]), "hasOffset" : true, "offsetDistance" : 1 * mm, "hasDraft" : true, "draftAngle" : 1 * degree, "draftPullDirection" : true});
        }
        {
            var Q0;
            Q0=makeQuery(id+"F23.boolean.opBoolean","INTERSECT",EDGE,{"derivedFrom":[makeQuery(id+"F21.opExtrude","SWEPT_FACE",FACE,{"disambiguationData":[OSD([sQuery(id+"F20.wireOp",EDGE,"E39.0")])]}),makeQuery(id+"F23.opExtrude","SWEPT_FACE",FACE,{"disambiguationData":[OSD([sQuery(id+"F22.wireOp",EDGE,"E42")])]})]});
            fillet(context, id + "F42", {"entities" : qUnion([Q0]), "radius" : .5 * mm, "tangentPropagation" : true, "allowEdgeOverflow" : false});
        }
        {
            var Q0;
            Q0=makeQuery(id+"F35.boolean.opBoolean","COPY",FACE,{"derivedFrom":makeQuery(id+"F35.opExtrude","SWEPT_FACE",FACE,{"disambiguationData":[OSD([sQuery(id+"F20.wireOp",EDGE,"E40.9")])]})});
            var sketch = newSketch(context, id + "F43", { "sketchPlane" : qUnion([Q0])});
            skCircle(sketch, "E62", {"center": v(32.75, 2.6) * mm, "radius": 2.45 * mm, "construction": true});
            skEllipticalArc(sketch, "E63.0", {"construction": true});
            skLineSegment(sketch, "E64", {"start": v(32.75, 0.15) * mm, "end": v(32.75, 13.43) * mm, "construction": true});
            skCircle(sketch, "E65", {"center": v(32.75, 2.6) * mm, "radius": 2.05 * mm});
            const initialGuessF43  = {"E63.0": [0.03275, -0.09596723813539623, 0, -1, 0.09611463872501952, 0.0961, 3.0712954359205873, 3.211889871258989]};
            skSetInitialGuess(sketch, initialGuessF43);
            skSolve(sketch);
        }
        {
            var Q0;
            Q0 = qSketchRegion(id + "F43", true);
            extrude(context, id + "F44", {"entities" : qUnion([Q0]), "operationType" : NewBodyOperationType.REMOVE, "oppositeDirection" : true, "depth" : 25 * mm, "offsetDistance" : 25 * mm, "hasSecondDirection" : true, "secondDirectionOppositeDirection" : false, "secondDirectionDepth" : 25 * mm});
        }
        {
            var Q0;
            Q0=makeQuery(id+"F21.opExtrude","CAP_FACE",FACE,{"disambiguationData":[OSD([sQuery(id+"F20.wireOp",EDGE,"E39.0"),sQuery(id+"F20.wireOp",EDGE,"E39.1"),sQuery(id+"F20.wireOp",EDGE,"E39.2"),sQuery(id+"F20.wireOp",EDGE,"E39.3"),sQuery(id+"F20.wireOp",EDGE,"E39.4"),sQuery(id+"F20.wireOp",EDGE,"E39.5"),sQuery(id+"F20.wireOp",EDGE,"E39.6"),sQuery(id+"F20.wireOp",EDGE,"E39.7"),sQuery(id+"F20.wireOp",EDGE,"E39.8"),sQuery(id+"F20.wireOp",EDGE,"E39.9"),sQuery(id+"F20.wireOp",EDGE,"E39.10"),sQuery(id+"F20.wireOp",EDGE,"E39.11")])],"isStart":true});
            cPlane(context, id + "F45", {"entities" : qUnion([Q0]), "cplaneType" : CPlaneType.OFFSET, "offset" : 5 * mm, "width" : 150 * mm, "height" : 150 * mm});
        }
    });
